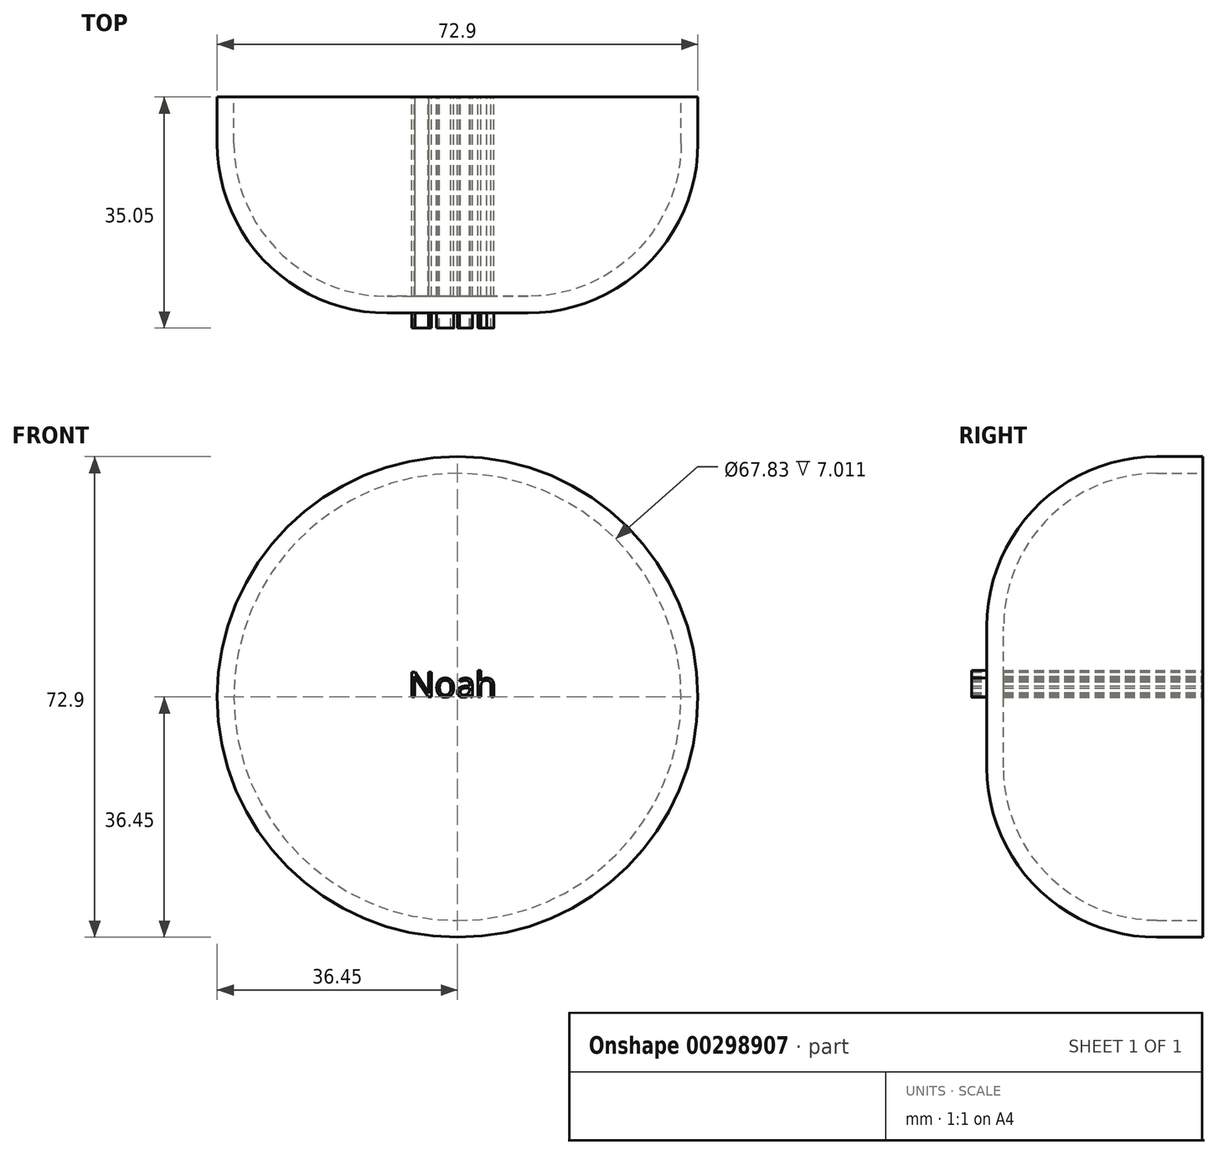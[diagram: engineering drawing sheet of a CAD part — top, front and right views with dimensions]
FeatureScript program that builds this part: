
annotation { "Feature Type Name" : "Feature", "Feature Type Description" : "" }
export const myFeature = defineFeature(function(context is Context, id is Id, definition is map)
    precondition{}
    {
        {
            var Q0;
            Q0=qCreatedBy(makeId("Front.planeOp"),FACE);
            var sketch = newSketch(context, id + "F0", { "sketchPlane" : qUnion([Q0])});
            skCircle(sketch, "E0", {"center": v(0, 0) * mm, "radius": 36.45 * mm});
            skSolve(sketch);
        }
        {
            var Q0;
            Q0=makeQuery(id+"F0.imprint","IMPRINT",FACE,{"disambiguationData":[TD([[makeQuery(id+"F0.imprint","IMPRINT",EDGE,{"derivedFrom":sQuery(id+"F0.wireOp",EDGE,"E0")}),1.0]])]});
            extrude(context, id + "F1", {"entities" : qUnion([Q0]), "depth" : 32.77 * mm});
        }
        {
            var Q0;
            Q0=makeQuery(id+"F1.opExtrude","CAP_EDGE",EDGE,{"disambiguationData":[OSD([sQuery(id+"F0.wireOp",EDGE,"E0")])],"isStart":false});
            fillet(context, id + "F2", {"entities" : qUnion([Q0]), "radius" : 25.75 * mm, "tangentPropagation" : true, "allowEdgeOverflow" : false});
        }
        {
            var Q0;
            Q0=makeQuery(id+"F1.opExtrude","CAP_FACE",FACE,{"disambiguationData":[OSD([sQuery(id+"F0.wireOp",EDGE,"E0")])],"isStart":true});
            shell(context, id + "F3", {"entities" : qUnion([Q0]), "thickness" : 2.54 * mm});
        }
        {
            var Q0;
            Q0=qCreatedBy(makeId("Front.planeOp"),FACE);
            var sketch = newSketch(context, id + "F4", { "sketchPlane" : qUnion([Q0])});
            skText(sketch, "E1", { "text": "Noah", "fontName": "OpenSans-Regular.ttf"});
            const initialGuessF4  = {"E1": [-0.00744, 0, 1, 0, 0.0038]};
            skSetInitialGuess(sketch, initialGuessF4);
            skSolve(sketch);
        }
        {
            var Q0;
            Q0 = qSketchRegion(id + "F4", true);
            extrude(context, id + "F5", {"entities" : qUnion([Q0]), "operationType" : NewBodyOperationType.ADD, "depth" : 35.05 * mm});
        }
    });
